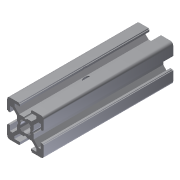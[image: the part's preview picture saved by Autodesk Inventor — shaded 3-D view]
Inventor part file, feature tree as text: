
AUTODESK INVENTOR PART (.ipt)
format: ipt  version: 2011 (Build 150239000, 239)  size: 236,032 bytes
history: native  units: in
note: dims shown in document units (in); Inventor stores cm internally (conversion verified against a paired STEP export)
features: plane x4, sketch x3, extrude x1, hole x1
ambient origin geometry x8: Origin, YZ Plane, XZ Plane, XY Plane, X Axis, Y Axis, Z Axis, Center Point
bodies: Solid1 (feature_tree)
feature tree (9):
  extrude  "Extrusion1"  TaperAngle=0.0deg  [1 undecoded]
  plane  "Work Plane1"
  plane  "Work Plane2"
  plane  "Work Plane3"
  sketch  "Sketch2"  dims[d3=0.0in d4=0.3937in]
  plane  "Work Plane4"
  hole  "Hole1"  [1 undecoded]
  sketch  "Sketch1"  dims[d0=2.7874in d1=0.0in d2=0.0in]
  sketch  "Sketch3"  dims[d5=0.25in d6=0.75in d7=0.375in d8=0.25in d9=0.5635in d10=1.0in d11=0.8108in]
note: 2 required parameter values undecoded (feature->parameter linkage not recoverable at this tier; creation-order binding heuristic only, values carry confidence <= 0.55)
